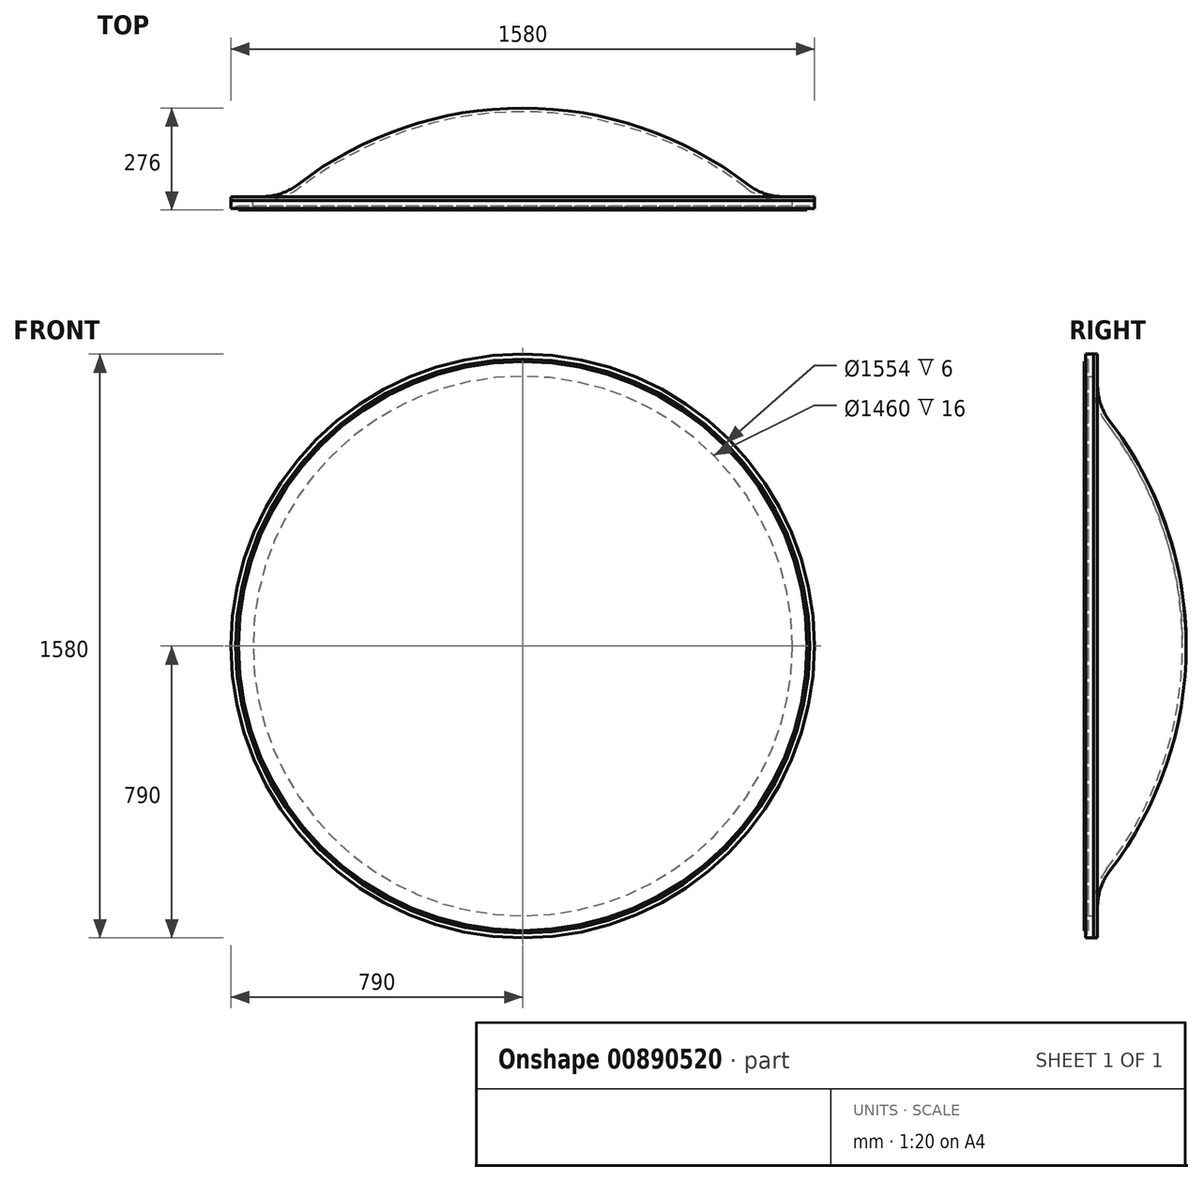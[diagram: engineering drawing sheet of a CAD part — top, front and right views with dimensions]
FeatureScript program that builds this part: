
annotation { "Feature Type Name" : "Feature", "Feature Type Description" : "" }
export const myFeature = defineFeature(function(context is Context, id is Id, definition is map)
    precondition{}
    {
        {
            var Q0;
            Q0=qCreatedBy(makeId("Right.planeOp"),FACE);
            var sketch = newSketch(context, id + "F0", { "sketchPlane" : qUnion([Q0])});
            skLineSegment(sketch, "E0", {"start": v(-10, 0) * mm, "end": v(-1885.79, 0) * mm, "construction": true});
            skArc(sketch, "E1", {"start": v(240, 0) * mm, "mid": v(186.86, 321.63) * mm, "end": v(33.1, 609.09) * mm});
            skArc(sketch, "E2", {"start": v(33.1, 609.09) * mm, "mid": v(8.5, 655.08) * mm, "end": v(0, 706.54) * mm});
            skLineSegment(sketch, "E3", {"start": v(0, 706.54) * mm, "end": v(0, 790) * mm});
            skLineSegment(sketch, "E4.0", {"start": v(-10, 706.54) * mm, "end": v(-10, 790) * mm});
            skArc(sketch, "E4.1", {"start": v(25.17, 603) * mm, "mid": v(-0.97, 651.86) * mm, "end": v(-10, 706.54) * mm});
            skArc(sketch, "E4.2", {"start": v(230, 0) * mm, "mid": v(177.4, 318.42) * mm, "end": v(25.17, 603) * mm});
            skLineSegment(sketch, "E5", {"start": v(0, 790) * mm, "end": v(-10, 790) * mm});
            skLineSegment(sketch, "E6", {"start": v(240, 0) * mm, "end": v(230, 0) * mm});
            skSolve(sketch);
        }
        {
            var Q0;
            Q0 = qSketchRegion(id + "F0", true);
            var Q1;
            Q1=sQuery(id+"F0.wireOp",EDGE,"E0");
            revolve(context, id + "F1", {"surfaceOperationType" : NewSurfaceOperationType.NEW, "entities" : qUnion([Q0]), "axis" : qUnion([Q1]), "revolveType" : RevolveType.FULL});
        }
        {
            var Q0;
            Q0=qCreatedBy(makeId("Right.planeOp"),FACE);
            var sketch = newSketch(context, id + "F2", { "sketchPlane" : qUnion([Q0])});
            skLineSegment(sketch, "E7", {"start": v(-10, 790) * mm, "end": v(-32, 790) * mm});
            skLineSegment(sketch, "E8", {"start": v(-32, 790) * mm, "end": v(-32, 777) * mm});
            skLineSegment(sketch, "E9", {"start": v(-32, 777) * mm, "end": v(-26, 777) * mm});
            skLineSegment(sketch, "E10", {"start": v(-26, 777) * mm, "end": v(-26, 730) * mm});
            skLineSegment(sketch, "E11", {"start": v(-26, 730) * mm, "end": v(-10, 730) * mm});
            skLineSegment(sketch, "E12", {"start": v(-10, 730) * mm, "end": v(-10, 790) * mm});
            skSolve(sketch);
        }
        {
            var Q0;
            Q0 = qSketchRegion(id + "F2", true);
            var Q1;
            Q1=sQuery(id+"F0.wireOp",EDGE,"E0");
            revolve(context, id + "F3", {"surfaceOperationType" : NewSurfaceOperationType.NEW, "entities" : qUnion([Q0]), "axis" : qUnion([Q1]), "revolveType" : RevolveType.FULL});
        }
        {
            var Q0;
            Q0=qCreatedBy(makeId("Right.planeOp"),FACE);
            var sketch = newSketch(context, id + "F4", { "sketchPlane" : qUnion([Q0])});
            skLineSegment(sketch, "E13.bottom", {"start": v(-26, 0) * mm, "end": v(-36, 0) * mm});
            skLineSegment(sketch, "E13.top", {"start": v(-26, 770) * mm, "end": v(-36, 770) * mm});
            skLineSegment(sketch, "E13.left", {"start": v(-26, 0) * mm, "end": v(-26, 770) * mm});
            skLineSegment(sketch, "E13.right", {"start": v(-36, 0) * mm, "end": v(-36, 770) * mm});
            skLineSegment(sketch, "E14", {"start": v(0, 0) * mm, "end": v(377.78, 0) * mm, "construction": true});
            skSolve(sketch);
        }
        {
            var Q0;
            Q0=makeQuery(id+"F4.imprint","IMPRINT",FACE,{"disambiguationData":[TD([[makeQuery(id+"F4.imprint","IMPRINT",EDGE,{"derivedFrom":sQuery(id+"F4.wireOp",EDGE,"E13.bottom")}),-1.0]])]});
            var Q1;
            Q1=sQuery(id+"F0.wireOp",EDGE,"E0");
            revolve(context, id + "F5", {"surfaceOperationType" : NewSurfaceOperationType.NEW, "entities" : qUnion([Q0]), "axis" : qUnion([Q1]), "revolveType" : RevolveType.FULL});
        }
    });
